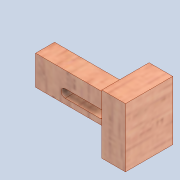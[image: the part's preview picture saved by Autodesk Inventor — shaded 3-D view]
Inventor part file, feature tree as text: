
AUTODESK INVENTOR PART (.ipt)
format: ipt  version: 2020 (Build 240168000, 168)  size: 159,232 bytes
history: native  units: mm
features: extrude x4, sketch x4, fillet x1
ambient origin geometry x8: Origin, YZ Plane, XZ Plane, XY Plane, X Axis, Y Axis, Z Axis, Center Point
bodies: Solid1 (feature_tree)
feature tree (9):
  extrude  "Extrusion1"  Depth=25.0mm
  extrude  "Extrusion5"  Depth=3.5mm
  extrude  "Extrusion6"  Depth=4.0mm
  extrude  "Extrusion7"  Depth=2.0mm
  fillet  "Fillet2"  Radius=15.0mm
  sketch  "Sketch1"  dims[d0=50.0mm d1=25.0mm]
  sketch  "Sketch5"  dims[d2=20.0mm d3=0.0mm d29=3.5mm]
  sketch  "Sketch6"  dims[d30=4.0mm d31=4.0mm]
  sketch  "Sketch7"  dims[d32=20.0mm d33=15.0mm d34=15.0mm d35=0.0mm d36=10.0mm d37=10.0mm d38=0.0mm d40=12.0mm d41=0.0mm d42=2.0mm]
